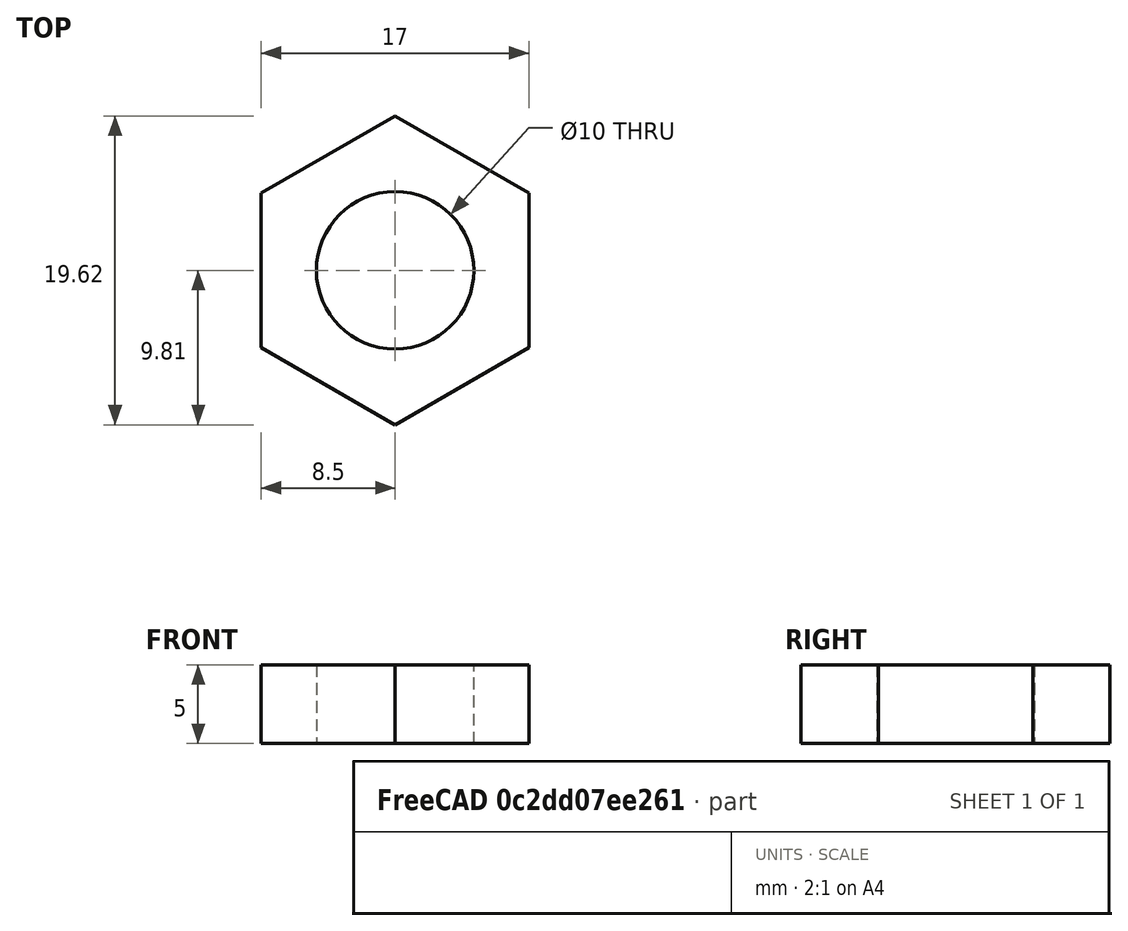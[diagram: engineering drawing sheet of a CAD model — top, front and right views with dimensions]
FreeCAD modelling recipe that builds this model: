
FCSTD DOCUMENT  (FreeCAD 0.19R24276 (Git))
Label: M10x8_gaika
License: All rights reserved
LicenseURL: http://en.wikipedia.org/wiki/All_rights_reserved
objects: Sketcher::SketchObject×1, PartDesign::Pad×1, PartDesign::Body×1
note: 4 computed .brp shape members not serialized (recipe doc carries the construction recipe); baked Part::Feature solids carry a one-line shape summary decoded from their .brp

FEATURE [Sketcher::SketchObject] Sketch
  FullyConstrained = true
  MapMode = 5
  Support = -> [XY_Plane]
  sketch-geometry (13):
    g0: Circle CenterX=0 CenterY=0 CenterZ=0 NormalX=0 NormalY=0 NormalZ=1 AngleXU=0 Radius=5
    g1: LineSegment StartX=-1.676e-13 StartY=-9.81495 StartZ=0 EndX=8.5 EndY=-4.90748 EndZ=0
    g2: LineSegment StartX=8.5 StartY=-4.90748 StartZ=0 EndX=8.5 EndY=4.90748 EndZ=0
    g3: LineSegment StartX=8.5 StartY=4.90748 StartZ=0 EndX=-1.67e-13 EndY=9.81495 EndZ=0
    g4: LineSegment StartX=-1.676e-13 StartY=9.81495 StartZ=0 EndX=-8.5 EndY=4.90748 EndZ=0
    g5: LineSegment StartX=-8.5 StartY=4.90748 StartZ=0 EndX=-8.5 EndY=-4.90748 EndZ=0
    g6: LineSegment StartX=-8.5 StartY=-4.90748 StartZ=0 EndX=-1.67e-13 EndY=-9.81495 EndZ=0
    g7: LineSegment StartX=-8.5 StartY=4.90748 StartZ=0 EndX=8.5 EndY=-4.90748 EndZ=0
    g8: LineSegment StartX=-8.5 StartY=-4.90748 StartZ=0 EndX=8.5 EndY=4.90748 EndZ=0
    g9: LineSegment StartX=-1.676e-13 StartY=9.81495 StartZ=0 EndX=-1.676e-13 EndY=-9.81495 EndZ=0
    g10: LineSegment StartX=8.5 StartY=-4.90748 StartZ=0 EndX=0 EndY=0 EndZ=0
    g11: LineSegment StartX=0 StartY=0 StartZ=0 EndX=-1.676e-13 EndY=9.81495 EndZ=0
    g12: LineSegment StartX=0 StartY=0 StartZ=0 EndX=-8.5 EndY=-4.90748 EndZ=0
  constraints (28):
    c: Coincident(g0,g-1)
    c: Diameter(g0) = 10
    c: Coincident(g1,g2)
    c: Coincident(g2,g3)
    c: Coincident(g3,g4)
    c: Coincident(g4,g5)
    c: Coincident(g5,g6)
    c: Coincident(g6,g1)
    c: Equal(g1, g2-g6) x5
    c: Distance(g3,g1) = 17
    c: Parallel(g4,g1)
    c: Coincident(g7,g4)
    c: Coincident(g7,g1)
    c: Coincident(g8,g5)
    c: Coincident(g8,g2)
    c: Coincident(g9,g3)
    c: Coincident(g9,g1)
    c: Vertical(g9)
    c: Equal(g8,g9)
    c: Equal(g9,g7)
    c: Coincident(g10,g1)
    c: Coincident(g10,g0)
    c: Coincident(g11,g0)
    c: Coincident(g11,g3)
    c: Equal(g11,g10)
    c: Coincident(g12,g0)
    c: Coincident(g12,g5)
    c: Equal(g12,g10)
FEATURE [PartDesign::Pad] Pad
  Direction = (1,1,1)
  Length = 5
  Length2 = 100
  Profile = -> Sketch
  Type = 0
FEATURE [PartDesign::Body] Body
  Group = -> [Sketch,Pad]
  Origin = -> Origin
  Tip = -> Pad
